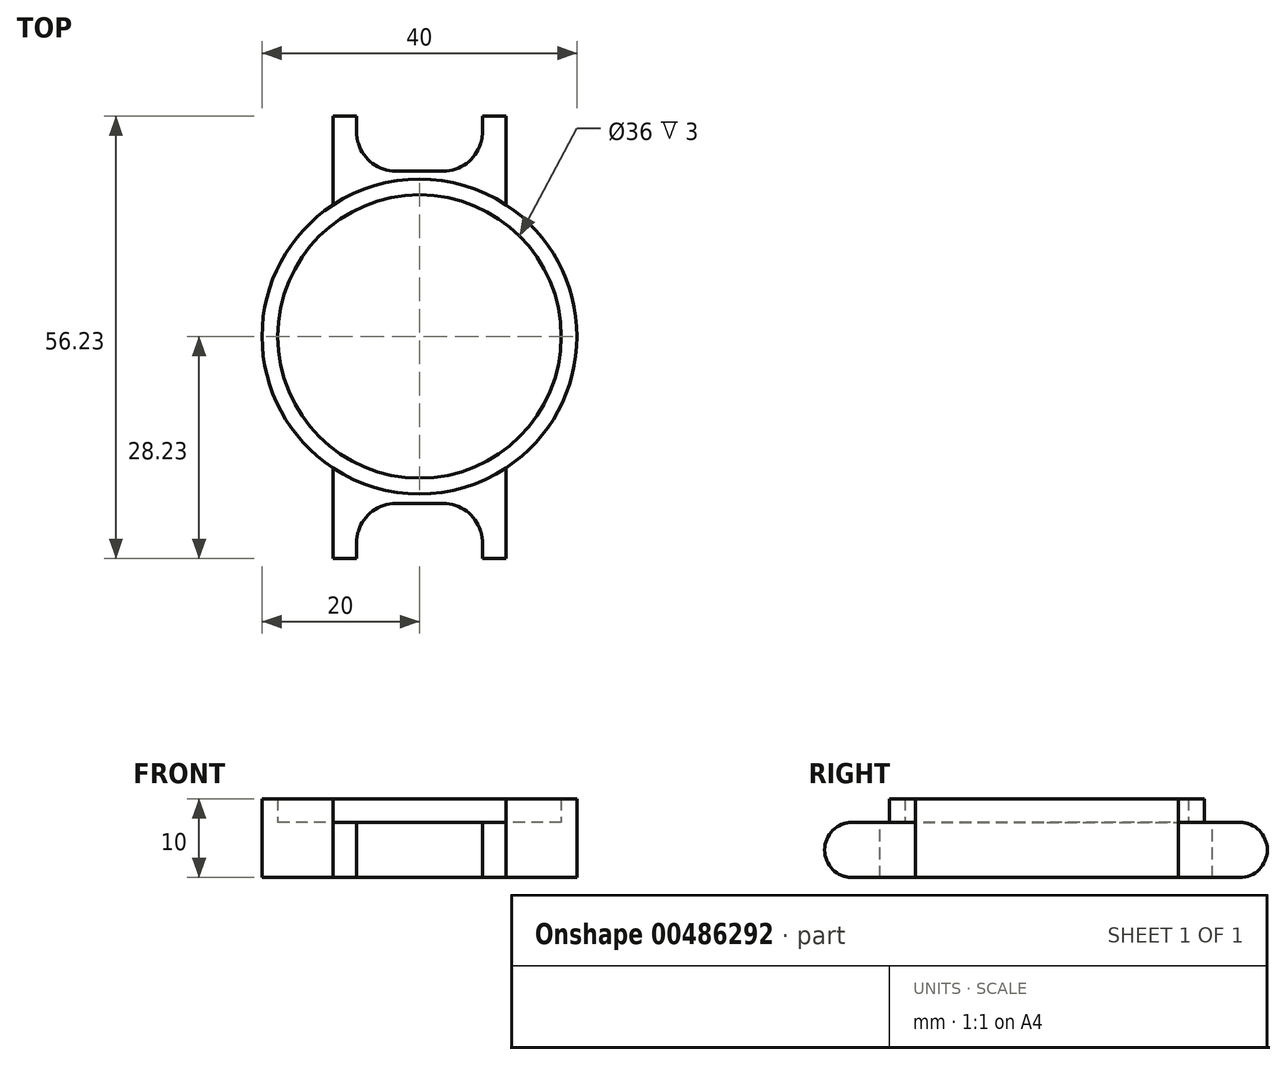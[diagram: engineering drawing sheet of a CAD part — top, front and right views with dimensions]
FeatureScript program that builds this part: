
annotation { "Feature Type Name" : "Feature", "Feature Type Description" : "" }
export const myFeature = defineFeature(function(context is Context, id is Id, definition is map)
    precondition{}
    {
        {
            var Q0;
            Q0=qCreatedBy(makeId("Top.planeOp"),FACE);
            var sketch = newSketch(context, id + "F0", { "sketchPlane" : qUnion([Q0])});
            skCircle(sketch, "E0", {"center": v(0, 0) * mm, "radius": 20 * mm});
            skLineSegment(sketch, "E1.bottom", {"start": v(11, 12) * mm, "end": v(-11, 12) * mm});
            skLineSegment(sketch, "E1.top", {"start": v(11, 28) * mm, "end": v(-11, 28) * mm});
            skLineSegment(sketch, "E1.left", {"start": v(11, 12) * mm, "end": v(11, 28) * mm});
            skLineSegment(sketch, "E1.right", {"start": v(-11, 12) * mm, "end": v(-11, 28) * mm});
            skPoint(sketch, "E1.middle", {"position": v(0, 20) * mm});
            skLineSegment(sketch, "E2.bottom", {"start": v(11, -28.23) * mm, "end": v(-11, -28.23) * mm});
            skLineSegment(sketch, "E2.top", {"start": v(11, -11.77) * mm, "end": v(-11, -11.77) * mm});
            skLineSegment(sketch, "E2.left", {"start": v(11, -28.23) * mm, "end": v(11, -11.77) * mm});
            skLineSegment(sketch, "E2.right", {"start": v(-11, -28.23) * mm, "end": v(-11, -11.77) * mm});
            skPoint(sketch, "E2.middle", {"position": v(0, -20) * mm});
            skSolve(sketch);
        }
        {
            var Q0;
            Q0 = qSketchRegion(id + "F0", true);
            extrude(context, id + "F1", {"entities" : qUnion([Q0]), "depth" : 7 * mm, "offsetDistance" : 25 * mm});
        }
        {
            var Q0;
            Q0=makeQuery(id+"F1.opExtrude","CAP_FACE",FACE,{"disambiguationData":[OSD([sQuery(id+"F0.wireOp",EDGE,"E0"),sQuery(id+"F0.wireOp",EDGE,"E1.top"),sQuery(id+"F0.wireOp",EDGE,"E1.left"),sQuery(id+"F0.wireOp",EDGE,"E1.right"),sQuery(id+"F0.wireOp",EDGE,"E2.bottom"),sQuery(id+"F0.wireOp",EDGE,"E2.left"),sQuery(id+"F0.wireOp",EDGE,"E2.right")])],"isStart":false});
            var sketch = newSketch(context, id + "F2", { "sketchPlane" : qUnion([Q0])});
            skLineSegment(sketch, "E3.bottom", {"start": v(-8, 28) * mm, "end": v(8, 28) * mm});
            skLineSegment(sketch, "E3.top", {"start": v(-8, 21) * mm, "end": v(8, 21) * mm});
            skLineSegment(sketch, "E3.left", {"start": v(-8, 28) * mm, "end": v(-8, 21) * mm});
            skLineSegment(sketch, "E3.right", {"start": v(8, 28) * mm, "end": v(8, 21) * mm});
            skLineSegment(sketch, "E4.bottom", {"start": v(-8, -28.23) * mm, "end": v(8, -28.23) * mm});
            skLineSegment(sketch, "E4.top", {"start": v(-8, -21.23) * mm, "end": v(8, -21.23) * mm});
            skLineSegment(sketch, "E4.left", {"start": v(-8, -28.23) * mm, "end": v(-8, -21.23) * mm});
            skLineSegment(sketch, "E4.right", {"start": v(8, -28.23) * mm, "end": v(8, -21.23) * mm});
            skSolve(sketch);
        }
        {
            var Q0;
            Q0 = qSketchRegion(id + "F2", true);
            extrude(context, id + "F3", {"entities" : qUnion([Q0]), "operationType" : NewBodyOperationType.REMOVE, "oppositeDirection" : true, "depth" : 10 * mm, "offsetDistance" : 25 * mm});
        }
        {
            var Q0;
            Q0=makeQuery(id+"F3.boolean.opBoolean","COPY",EDGE,{"derivedFrom":makeQuery(id+"F3.opExtrude","SWEPT_EDGE",EDGE,{"disambiguationData":[OSD([sQuery(id+"F2.wireOp",EDGE,"E3.top"),sQuery(id+"F2.wireOp",EDGE,"E3.left")])]})});
            var Q1;
            Q1=makeQuery(id+"F3.boolean.opBoolean","COPY",EDGE,{"derivedFrom":makeQuery(id+"F3.opExtrude","SWEPT_EDGE",EDGE,{"disambiguationData":[OSD([sQuery(id+"F2.wireOp",EDGE,"E3.top"),sQuery(id+"F2.wireOp",EDGE,"E3.right")])]})});
            var Q2;
            Q2=makeQuery(id+"F3.boolean.opBoolean","COPY",EDGE,{"derivedFrom":makeQuery(id+"F3.opExtrude","SWEPT_EDGE",EDGE,{"disambiguationData":[OSD([sQuery(id+"F2.wireOp",EDGE,"E4.top"),sQuery(id+"F2.wireOp",EDGE,"E4.right")])]})});
            var Q3;
            Q3=makeQuery(id+"F3.boolean.opBoolean","COPY",EDGE,{"derivedFrom":makeQuery(id+"F3.opExtrude","SWEPT_EDGE",EDGE,{"disambiguationData":[OSD([sQuery(id+"F2.wireOp",EDGE,"E4.top"),sQuery(id+"F2.wireOp",EDGE,"E4.left")])]})});
            fillet(context, id + "F4", {"entities" : qUnion([Q0, Q1, Q2, Q3]), "radius" : 5 * mm, "tangentPropagation" : true, "allowEdgeOverflow" : false});
        }
        {
            var Q0;
            {var subQ0=sQuery(id+"F0.wireOp",EDGE,"E2.right");var subQ1=sQuery(id+"F0.wireOp",EDGE,"E2.bottom");Q0=makeQuery(id+"F3.boolean.opBoolean","SPLIT",EDGE,{"disambiguationData":[TD([makeQuery(id+"F1.opExtrude","SWEPT_FACE",FACE,{"disambiguationData":[OSD([subQ0])]})])],"derivedFrom":makeQuery(id+"F1.opExtrude","CAP_EDGE",EDGE,{"disambiguationData":[OSD([subQ1])],"isStart":false})});}
            var Q1;
            {var subQ0=sQuery(id+"F0.wireOp",EDGE,"E2.left");var subQ1=sQuery(id+"F0.wireOp",EDGE,"E2.bottom");Q1=makeQuery(id+"F3.boolean.opBoolean","SPLIT",EDGE,{"disambiguationData":[TD([makeQuery(id+"F1.opExtrude","SWEPT_FACE",FACE,{"disambiguationData":[OSD([subQ0])]})])],"derivedFrom":makeQuery(id+"F1.opExtrude","CAP_EDGE",EDGE,{"disambiguationData":[OSD([subQ1])],"isStart":false})});}
            var Q2;
            {var subQ0=sQuery(id+"F0.wireOp",EDGE,"E1.right");var subQ1=sQuery(id+"F0.wireOp",EDGE,"E1.top");Q2=makeQuery(id+"F3.boolean.opBoolean","SPLIT",EDGE,{"disambiguationData":[TD([makeQuery(id+"F1.opExtrude","SWEPT_FACE",FACE,{"disambiguationData":[OSD([subQ0])]})])],"derivedFrom":makeQuery(id+"F1.opExtrude","CAP_EDGE",EDGE,{"disambiguationData":[OSD([subQ1])],"isStart":false})});}
            var Q3;
            {var subQ0=sQuery(id+"F0.wireOp",EDGE,"E1.left");var subQ1=sQuery(id+"F0.wireOp",EDGE,"E1.top");Q3=makeQuery(id+"F3.boolean.opBoolean","SPLIT",EDGE,{"disambiguationData":[TD([makeQuery(id+"F1.opExtrude","SWEPT_FACE",FACE,{"disambiguationData":[OSD([subQ0])]})])],"derivedFrom":makeQuery(id+"F1.opExtrude","CAP_EDGE",EDGE,{"disambiguationData":[OSD([subQ1])],"isStart":false})});}
            var Q4;
            {var subQ0=sQuery(id+"F0.wireOp",EDGE,"E1.right");var subQ1=sQuery(id+"F0.wireOp",EDGE,"E1.top");Q4=makeQuery(id+"F3.boolean.opBoolean","SPLIT",EDGE,{"disambiguationData":[TD([makeQuery(id+"F1.opExtrude","SWEPT_FACE",FACE,{"disambiguationData":[OSD([subQ0])]})])],"derivedFrom":makeQuery(id+"F1.opExtrude","CAP_EDGE",EDGE,{"disambiguationData":[OSD([subQ1])],"isStart":true})});}
            var Q5;
            {var subQ0=sQuery(id+"F0.wireOp",EDGE,"E1.left");var subQ1=sQuery(id+"F0.wireOp",EDGE,"E1.top");Q5=makeQuery(id+"F3.boolean.opBoolean","SPLIT",EDGE,{"disambiguationData":[TD([makeQuery(id+"F1.opExtrude","SWEPT_FACE",FACE,{"disambiguationData":[OSD([subQ0])]})])],"derivedFrom":makeQuery(id+"F1.opExtrude","CAP_EDGE",EDGE,{"disambiguationData":[OSD([subQ1])],"isStart":true})});}
            var Q6;
            {var subQ0=sQuery(id+"F0.wireOp",EDGE,"E2.right");var subQ1=sQuery(id+"F0.wireOp",EDGE,"E2.bottom");Q6=makeQuery(id+"F3.boolean.opBoolean","SPLIT",EDGE,{"disambiguationData":[TD([makeQuery(id+"F1.opExtrude","SWEPT_FACE",FACE,{"disambiguationData":[OSD([subQ0])]})])],"derivedFrom":makeQuery(id+"F1.opExtrude","CAP_EDGE",EDGE,{"disambiguationData":[OSD([subQ1])],"isStart":true})});}
            var Q7;
            {var subQ0=sQuery(id+"F0.wireOp",EDGE,"E2.left");var subQ1=sQuery(id+"F0.wireOp",EDGE,"E2.bottom");Q7=makeQuery(id+"F3.boolean.opBoolean","SPLIT",EDGE,{"disambiguationData":[TD([makeQuery(id+"F1.opExtrude","SWEPT_FACE",FACE,{"disambiguationData":[OSD([subQ0])]})])],"derivedFrom":makeQuery(id+"F1.opExtrude","CAP_EDGE",EDGE,{"disambiguationData":[OSD([subQ1])],"isStart":true})});}
            fillet(context, id + "F5", {"entities" : qUnion([Q0, Q1, Q2, Q3, Q4, Q5, Q6, Q7]), "radius" : 3.5 * mm, "tangentPropagation" : true, "allowEdgeOverflow" : false});
        }
        {
            var Q0;
            Q0=makeQuery(id+"F1.opExtrude","CAP_FACE",FACE,{"disambiguationData":[OSD([sQuery(id+"F0.wireOp",EDGE,"E0"),sQuery(id+"F0.wireOp",EDGE,"E1.top"),sQuery(id+"F0.wireOp",EDGE,"E1.left"),sQuery(id+"F0.wireOp",EDGE,"E1.right"),sQuery(id+"F0.wireOp",EDGE,"E2.bottom"),sQuery(id+"F0.wireOp",EDGE,"E2.left"),sQuery(id+"F0.wireOp",EDGE,"E2.right")])],"isStart":false});
            var sketch = newSketch(context, id + "F6", { "sketchPlane" : qUnion([Q0])});
            skCircle(sketch, "E5", {"center": v(0, 0) * mm, "radius": 20 * mm});
            skCircle(sketch, "E6", {"center": v(0, 0) * mm, "radius": 18 * mm});
            skSolve(sketch);
        }
        {
            var Q0;
            Q0=makeQuery(id+"F6.imprint","IMPRINT",FACE,{"disambiguationData":[TD([[makeQuery(id+"F6.imprint","IMPRINT",EDGE,{"derivedFrom":sQuery(id+"F6.wireOp",EDGE,"E6")}),-1.0]])]});
            extrude(context, id + "F7", {"entities" : qUnion([Q0]), "operationType" : NewBodyOperationType.ADD, "depth" : 3 * mm, "offsetDistance" : 25 * mm});
        }
    });
